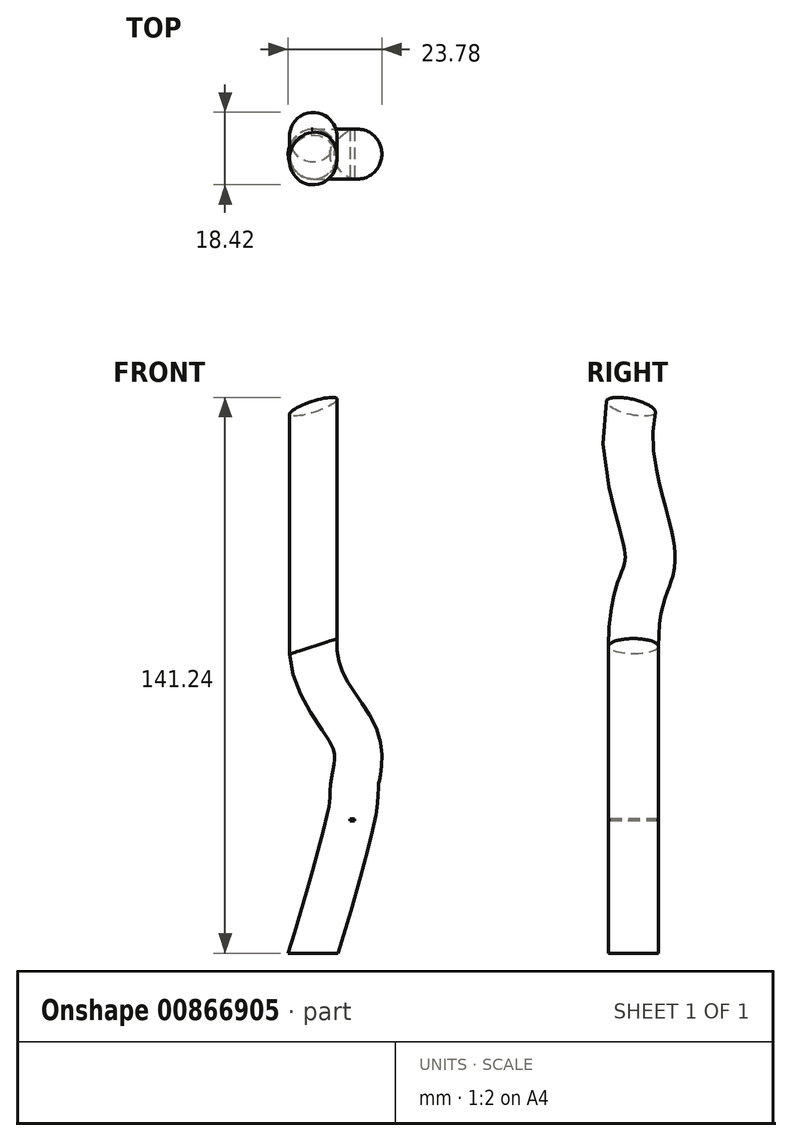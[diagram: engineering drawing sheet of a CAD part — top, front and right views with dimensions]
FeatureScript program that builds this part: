
annotation { "Feature Type Name" : "Feature", "Feature Type Description" : "" }
export const myFeature = defineFeature(function(context is Context, id is Id, definition is map)
    precondition{}
    {
        {
            var Q0;
            Q0=qCreatedBy(makeId("Front.planeOp"),FACE);
            var sketch = newSketch(context, id + "F0", { "sketchPlane" : qUnion([Q0])});
            skFitSpline(sketch, "E0", {"points": [v(0, 0) * mm, v(10.57, 43.1) * mm, v(10.57, 54.2) * mm, v(0, 77.98) * mm], "startDerivative": vector(83.17, 273.34) * mm, "endDerivative": vector(-1.8, 98.84) * mm});
            skSolve(sketch);
        }
        {
            var Q0;
            Q0=qCreatedBy(makeId("Right.planeOp"),FACE);
            var sketch = newSketch(context, id + "F1", { "sketchPlane" : qUnion([Q0])});
            skFitSpline(sketch, "E1", {"points": [v(0, 77.98) * mm, v(4.25, 101.16) * mm, v(-0.66, 138.85) * mm], "startDerivative": vector(0, 102.13) * mm, "endDerivative": vector(17.7, 75.55) * mm});
            skSolve(sketch);
        }
        {
            var Q0;
            Q0=qCreatedBy(makeId("Top.planeOp"),FACE);
            var sketch = newSketch(context, id + "F2", { "sketchPlane" : qUnion([Q0])});
            skCircle(sketch, "E2", {"center": v(0, 0) * mm, "radius": 6.35 * mm});
            skSolve(sketch);
        }
        {
            var Q0;
            Q0=makeQuery(id+"F2.imprint","IMPRINT",FACE,{"disambiguationData":[TD([[makeQuery(id+"F2.imprint","IMPRINT",EDGE,{"derivedFrom":sQuery(id+"F2.wireOp",EDGE,"E2")}),1.0]])]});
            var Q1;
            Q1=sQuery(id+"F0.wireOp",EDGE,"E0");
            sweep(context, id + "F3", {"profiles" : qUnion([Q0]), "path" : qUnion([Q1])});
        }
        {
            var Q0;
            Q0=makeQuery(id+"F3.opSweep","CAP_FACE",FACE,{"disambiguationData":[OSD([sQuery(id+"F0.wireOp",VERTEX,"E0.end"),sQuery(id+"F2.wireOp",EDGE,"E2")])],"isStart":false});
            var sketch = newSketch(context, id + "F4", { "sketchPlane" : qUnion([Q0])});
            skCircle(sketch, "E3", {"center": v(24.06, 0) * mm, "radius": 6.35 * mm});
            skSolve(sketch);
        }
        {
            var Q0;
            Q0=makeQuery(id+"F4.imprint","IMPRINT",FACE,{"disambiguationData":[TD([[makeQuery(id+"F4.imprint","IMPRINT",EDGE,{"derivedFrom":sQuery(id+"F4.wireOp",EDGE,"E3")}),1.0]])]});
            var Q1;
            Q1=sQuery(id+"F1.wireOp",EDGE,"E1");
            sweep(context, id + "F5", {"operationType" : NewBodyOperationType.ADD, "profiles" : qUnion([Q0]), "path" : qUnion([Q1])});
        }
        {
            var Q0;
            Q0=qCreatedBy(makeId("Front.planeOp"),FACE);
            var sketch = newSketch(context, id + "F6", { "sketchPlane" : qUnion([Q0])});
            skLineSegment(sketch, "E4.bottom", {"start": v(10.43, 33.57) * mm, "end": v(9.29, 33.57) * mm});
            skLineSegment(sketch, "E4.top", {"start": v(10.43, 34.08) * mm, "end": v(9.29, 34.08) * mm});
            skLineSegment(sketch, "E4.left", {"start": v(10.43, 33.57) * mm, "end": v(10.43, 34.08) * mm});
            skLineSegment(sketch, "E4.right", {"start": v(9.29, 33.57) * mm, "end": v(9.29, 34.08) * mm});
            skSolve(sketch);
        }
        {
            var Q0;
            Q0 = qSketchRegion(id + "F6", true);
            extrude(context, id + "F7", {"entities" : qUnion([Q0]), "operationType" : NewBodyOperationType.REMOVE, "endBound" : BoundingType.SYMMETRIC, "oppositeDirection" : true, "depth" : 25.4 * mm, "offsetDistance" : 25.4 * mm});
        }
    });
